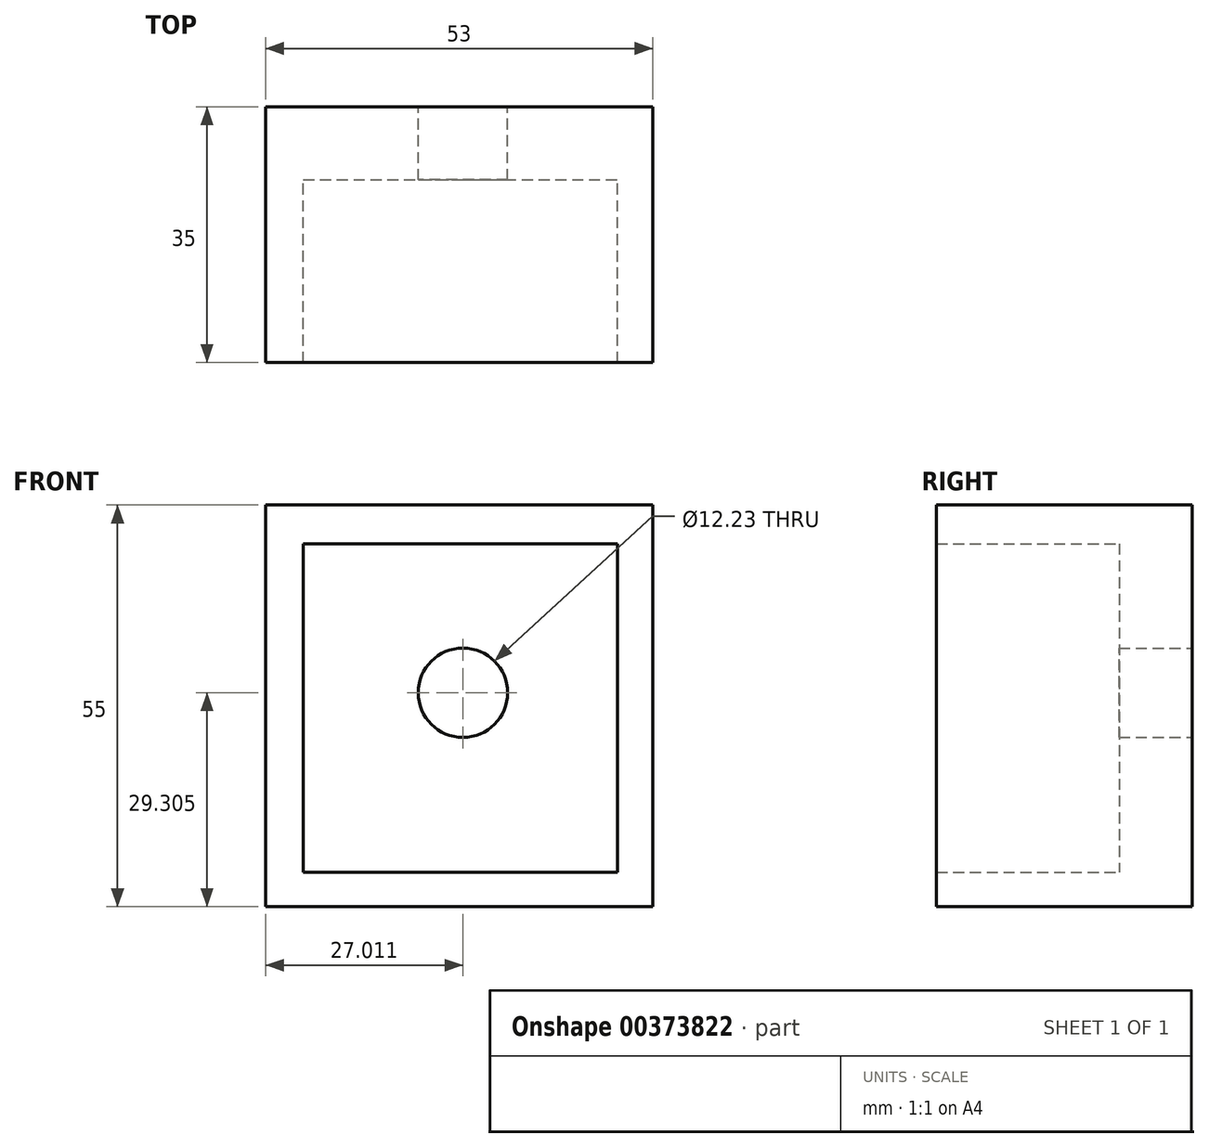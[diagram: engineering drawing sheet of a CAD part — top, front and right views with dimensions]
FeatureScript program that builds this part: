
annotation { "Feature Type Name" : "Feature", "Feature Type Description" : "" }
export const myFeature = defineFeature(function(context is Context, id is Id, definition is map)
    precondition{}
    {
        {
            var Q0;
            Q0=qCreatedBy(makeId("Front.planeOp"),FACE);
            var sketch = newSketch(context, id + "F0", { "sketchPlane" : qUnion([Q0])});
            skLineSegment(sketch, "E0.bottom", {"start": v(-45.98, 30.23) * mm, "end": v(7.02, 30.23) * mm});
            skLineSegment(sketch, "E0.top", {"start": v(-45.98, -24.77) * mm, "end": v(7.02, -24.77) * mm});
            skLineSegment(sketch, "E0.left", {"start": v(-45.98, 30.23) * mm, "end": v(-45.98, -24.77) * mm});
            skLineSegment(sketch, "E0.right", {"start": v(7.02, 30.23) * mm, "end": v(7.02, -24.77) * mm});
            skCircle(sketch, "E1", {"center": v(-18.96, 4.53) * mm, "radius": 6.15 * mm});
            skCircle(sketch, "E2", {"center": v(-18.96, 4.53) * mm, "radius": 6.08 * mm});
            skSolve(sketch);
        }
        {
            var Q0;
            Q0=makeQuery(id+"F0.imprint","IMPRINT",FACE,{"disambiguationData":[TD([[makeQuery(id+"F0.imprint","IMPRINT",EDGE,{"derivedFrom":sQuery(id+"F0.wireOp",EDGE,"E0.bottom")}),-1.0]])]});
            var sketch = newSketch(context, id + "F1", { "sketchPlane" : qUnion([Q0])});
            skLineSegment(sketch, "E3.bottom", {"start": v(-40.8, 24.94) * mm, "end": v(2.2, 24.94) * mm});
            skLineSegment(sketch, "E3.top", {"start": v(-40.8, -20.06) * mm, "end": v(2.2, -20.06) * mm});
            skLineSegment(sketch, "E3.left", {"start": v(-40.8, 24.94) * mm, "end": v(-40.8, -20.06) * mm});
            skLineSegment(sketch, "E3.right", {"start": v(2.2, 24.94) * mm, "end": v(2.2, -20.06) * mm});
            skCircle(sketch, "E4", {"center": v(-18.97, 4.54) * mm, "radius": 6.12 * mm});
            skSolve(sketch);
        }
        {
            var Q0;
            Q0=makeQuery(id+"F1.imprint","IMPRINT",FACE,{"disambiguationData":[TD([[makeQuery(id+"F1.imprint","IMPRINT",EDGE,{"derivedFrom":sQuery(id+"F1.wireOp",EDGE,"E3.bottom")}),1.0]])]});
            extrude(context, id + "F2", {"entities" : qUnion([Q0]), "depth" : 35 * mm});
        }
        {
            var Q0;
            Q0 = qSketchRegion(id + "F1", true);
            extrude(context, id + "F3", {"entities" : qUnion([Q0]), "operationType" : NewBodyOperationType.ADD, "depth" : 10 * mm});
        }
    });
